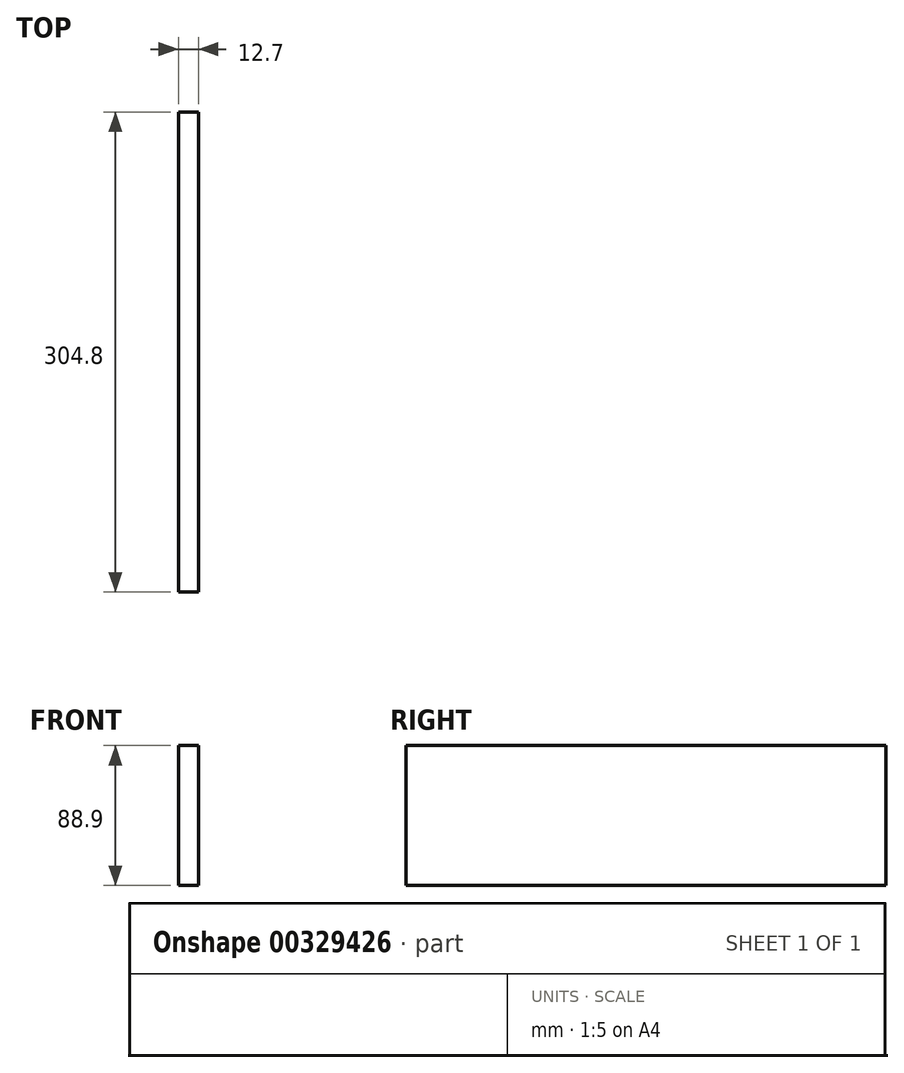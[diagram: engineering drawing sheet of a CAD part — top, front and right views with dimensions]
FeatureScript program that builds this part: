
annotation { "Feature Type Name" : "Feature", "Feature Type Description" : "" }
export const myFeature = defineFeature(function(context is Context, id is Id, definition is map)
    precondition{}
    {
        {
            var Q0;
            Q0=qCreatedBy(makeId("Right.planeOp"),FACE);
            var sketch = newSketch(context, id + "F0", { "sketchPlane" : qUnion([Q0])});
            skLineSegment(sketch, "E0.bottom", {"start": v(-152.4, 44.45) * mm, "end": v(152.4, 44.45) * mm});
            skLineSegment(sketch, "E0.top", {"start": v(-152.4, -44.45) * mm, "end": v(152.4, -44.45) * mm});
            skLineSegment(sketch, "E0.left", {"start": v(-152.4, 44.45) * mm, "end": v(-152.4, -44.45) * mm});
            skLineSegment(sketch, "E0.right", {"start": v(152.4, 44.45) * mm, "end": v(152.4, -44.45) * mm});
            skPoint(sketch, "E0.middle", {"position": v(0, 0) * mm});
            skSolve(sketch);
        }
        {
            var Q0;
            Q0=qSketchRegion(id+"F0",true);
            extrude(context, id + "F1", {"entities" : qUnion([Q0]), "depth" : 12.7 * mm});
        }
    });
